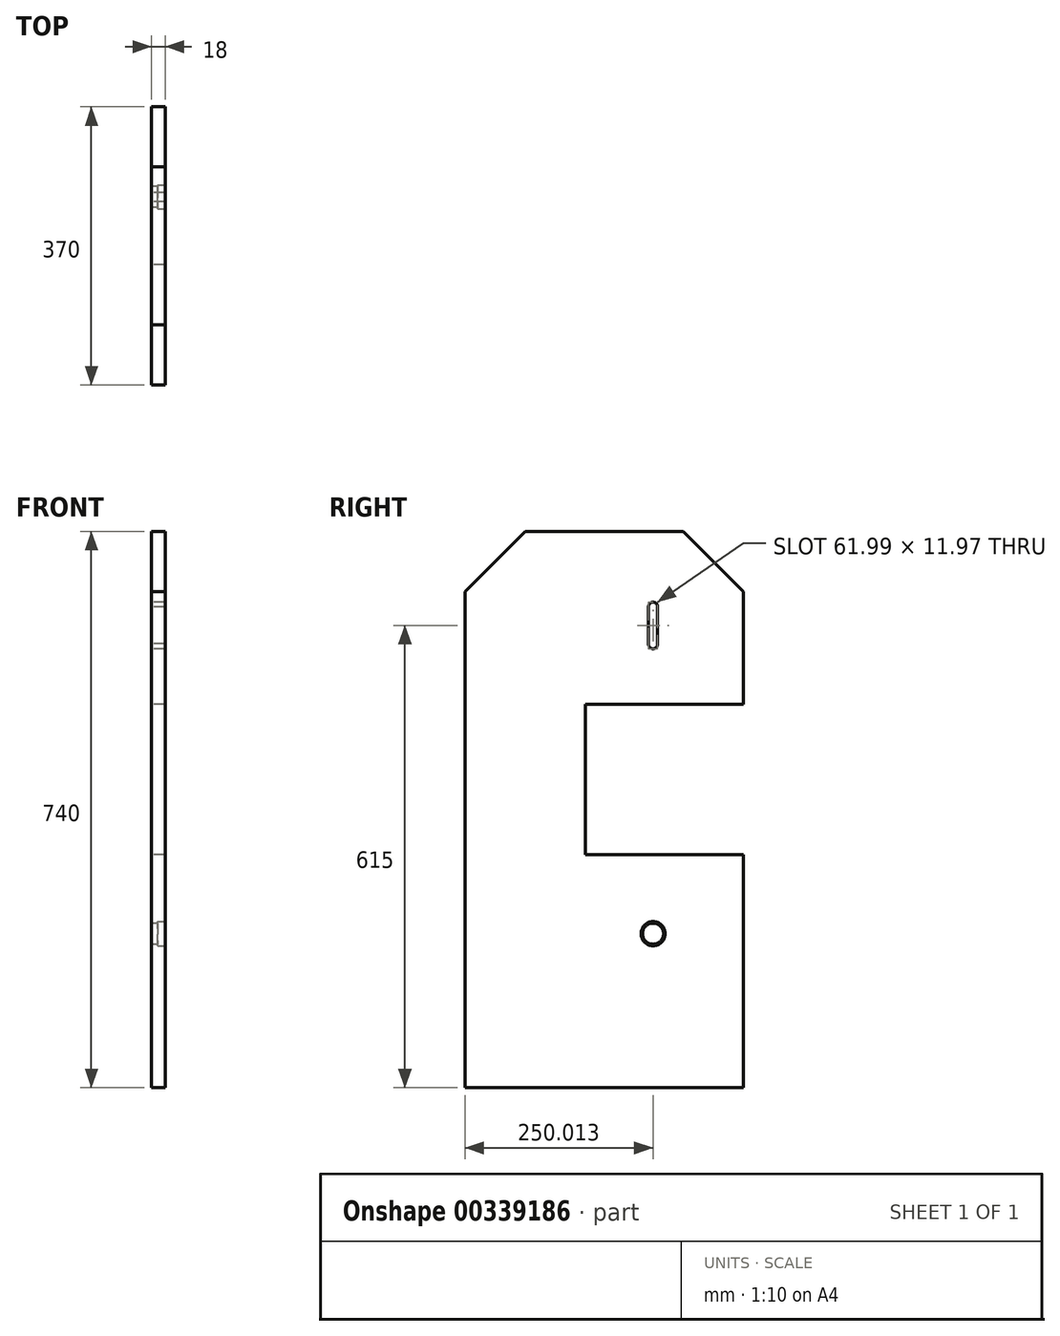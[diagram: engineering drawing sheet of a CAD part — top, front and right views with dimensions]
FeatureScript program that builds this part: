
annotation { "Feature Type Name" : "Feature", "Feature Type Description" : "" }
export const myFeature = defineFeature(function(context is Context, id is Id, definition is map)
    precondition{}
    {
        {
            var Q0;
            Q0=qCreatedBy(makeId("Right.planeOp"),FACE);
            var sketch = newSketch(context, id + "F0", { "sketchPlane" : qUnion([Q0])});
            skLineSegment(sketch, "E0", {"start": v(0, 0) * mm, "end": v(0, 740) * mm});
            skLineSegment(sketch, "E1", {"start": v(0, 740) * mm, "end": v(370, 740) * mm});
            skLineSegment(sketch, "E2", {"start": v(370, 740) * mm, "end": v(370, 510) * mm});
            skLineSegment(sketch, "E3", {"start": v(0, 0) * mm, "end": v(370, 0) * mm});
            skLineSegment(sketch, "E4", {"start": v(370, 0) * mm, "end": v(370, 310) * mm});
            skLineSegment(sketch, "E5", {"start": v(370, 310) * mm, "end": v(160, 310) * mm});
            skLineSegment(sketch, "E6", {"start": v(160, 310) * mm, "end": v(160, 510) * mm});
            skLineSegment(sketch, "E7", {"start": v(160, 510) * mm, "end": v(370, 510) * mm});
            skCircle(sketch, "E8", {"center": v(250, 205) * mm, "radius": 6 * mm});
            skArc(sketch, "E9", {"start": v(256, 640) * mm, "mid": v(249.72, 646) * mm, "end": v(244.03, 639.44) * mm});
            skArc(sketch, "E10", {"start": v(244.03, 590.56) * mm, "mid": v(249.72, 584) * mm, "end": v(256, 590) * mm});
            skLineSegment(sketch, "E11", {"start": v(244.03, 640.56) * mm, "end": v(244.03, 589.44) * mm});
            skLineSegment(sketch, "E12", {"start": v(256, 640) * mm, "end": v(256, 590) * mm});
            skSolve(sketch);
        }
        {
            var Q0;
            Q0 = qSketchRegion(id + "F0", true);
            extrude(context, id + "F1", {"entities" : qUnion([Q0]), "depth" : 18 * mm});
        }
        {
            var Q0;
            Q0=makeQuery(id+"F1.opExtrude","SWEPT_EDGE",EDGE,{"disambiguationData":[OSD([sQuery(id+"F0.wireOp",EDGE,"E0"),sQuery(id+"F0.wireOp",EDGE,"E1")])]});
            var Q1;
            Q1=makeQuery(id+"F1.opExtrude","SWEPT_EDGE",EDGE,{"disambiguationData":[OSD([sQuery(id+"F0.wireOp",EDGE,"E1"),sQuery(id+"F0.wireOp",EDGE,"E2")])]});
            chamfer(context, id + "F2", {"entities" : qUnion([Q0, Q1]), "width" : 80 * mm, "tangentPropagation" : true});
        }
        {
            var Q0;
            Q0=makeQuery(id+"F1.opExtrude","CAP_FACE",FACE,{"disambiguationData":[OSD([sQuery(id+"F0.wireOp",EDGE,"E0"),sQuery(id+"F0.wireOp",EDGE,"E1"),sQuery(id+"F0.wireOp",EDGE,"E2"),sQuery(id+"F0.wireOp",EDGE,"E3"),sQuery(id+"F0.wireOp",EDGE,"E4"),sQuery(id+"F0.wireOp",EDGE,"E5"),sQuery(id+"F0.wireOp",EDGE,"E6"),sQuery(id+"F0.wireOp",EDGE,"E7"),sQuery(id+"F0.wireOp",EDGE,"E8"),sQuery(id+"F0.wireOp",EDGE,"E9"),sQuery(id+"F0.wireOp",EDGE,"E10"),sQuery(id+"F0.wireOp",EDGE,"E11"),sQuery(id+"F0.wireOp",EDGE,"E12")])],"isStart":false});
            var sketch = newSketch(context, id + "F3", { "sketchPlane" : qUnion([Q0])});
            skCircle(sketch, "E13", {"center": v(250, 205) * mm, "radius": 16 * mm});
            skSolve(sketch);
        }
        {
            var Q0;
            Q0 = qSketchRegion(id + "F3", true);
            extrude(context, id + "F4", {"entities" : qUnion([Q0]), "operationType" : NewBodyOperationType.REMOVE, "oppositeDirection" : true, "depth" : 10 * mm});
        }
        {
            var Q0;
            Q0=makeQuery(id+"F1.opExtrude","CAP_FACE",FACE,{"disambiguationData":[OSD([sQuery(id+"F0.wireOp",EDGE,"E0"),sQuery(id+"F0.wireOp",EDGE,"E1"),sQuery(id+"F0.wireOp",EDGE,"E2"),sQuery(id+"F0.wireOp",EDGE,"E3"),sQuery(id+"F0.wireOp",EDGE,"E4"),sQuery(id+"F0.wireOp",EDGE,"E5"),sQuery(id+"F0.wireOp",EDGE,"E6"),sQuery(id+"F0.wireOp",EDGE,"E7"),sQuery(id+"F0.wireOp",EDGE,"E8"),sQuery(id+"F0.wireOp",EDGE,"E9"),sQuery(id+"F0.wireOp",EDGE,"E10"),sQuery(id+"F0.wireOp",EDGE,"E11"),sQuery(id+"F0.wireOp",EDGE,"E12")])],"isStart":true});
            var sketch = newSketch(context, id + "F5", { "sketchPlane" : qUnion([Q0])});
            skCircle(sketch, "E14", {"center": v(-250, 205) * mm, "radius": 14 * mm});
            skSolve(sketch);
        }
        {
            var Q0;
            Q0 = qSketchRegion(id + "F5", true);
            extrude(context, id + "F6", {"entities" : qUnion([Q0]), "operationType" : NewBodyOperationType.REMOVE, "oppositeDirection" : true, "depth" : 8 * mm});
        }
    });
